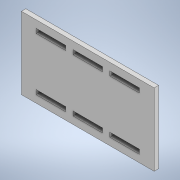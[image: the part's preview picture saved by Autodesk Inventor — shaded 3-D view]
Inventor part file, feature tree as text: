
AUTODESK INVENTOR PART (.ipt)
format: ipt  version: 2022 (Build 260153000, 153)  size: 133,632 bytes
history: native  units: mm
features: extrude x1, sketch x1
ambient origin geometry x8: Origin, YZ Plane, XZ Plane, XY Plane, X Axis, Y Axis, Z Axis, Center Point
bodies: Solid1 (feature_tree)
feature tree (2):
  extrude  "Extrusion1"  Depth=3.0mm TaperAngle=0.0deg
  sketch  "Sketch1"  dims[d3=49.0mm d4=3.0mm d5=0.0mm d6=5.0mm d7=10.0mm d8=20.0mm d11=20.0mm d14=5.0mm d17=24.5mm d19=20.0mm d20=5.0mm]
